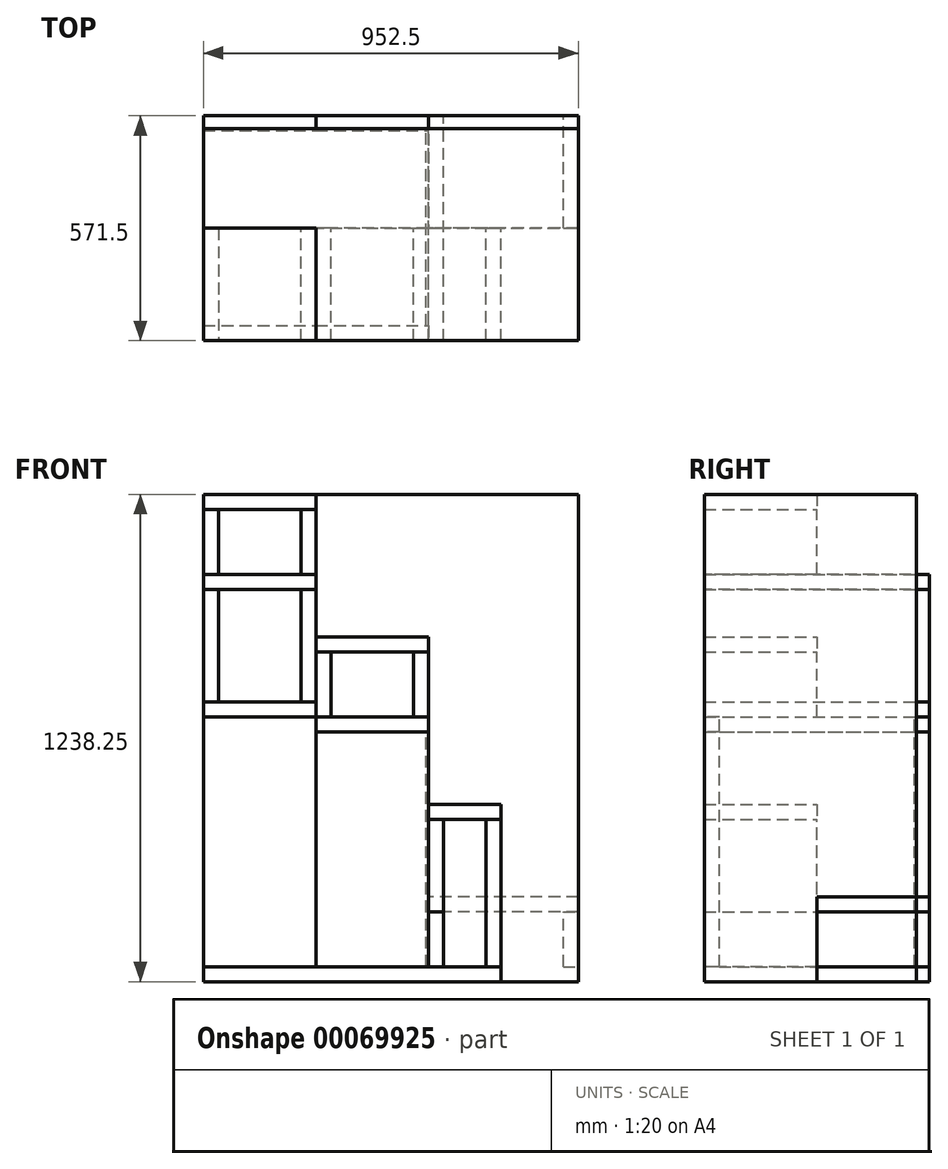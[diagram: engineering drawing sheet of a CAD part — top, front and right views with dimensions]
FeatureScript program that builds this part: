
annotation { "Feature Type Name" : "Feature", "Feature Type Description" : "" }
export const myFeature = defineFeature(function(context is Context, id is Id, definition is map)
    precondition{}
    {
        {
            var Q0;
            Q0=qCreatedBy(makeId("Top.planeOp"),FACE);
            var sketch = newSketch(context, id + "F0", { "sketchPlane" : qUnion([Q0])});
            skLineSegment(sketch, "E0.bottom", {"start": v(-476.25, 269.24) * mm, "end": v(476.25, 269.24) * mm});
            skLineSegment(sketch, "E0.top", {"start": v(-476.25, -269.24) * mm, "end": v(476.25, -269.24) * mm});
            skLineSegment(sketch, "E0.left", {"start": v(-476.25, 269.24) * mm, "end": v(-476.25, -269.24) * mm});
            skLineSegment(sketch, "E0.right", {"start": v(476.25, 269.24) * mm, "end": v(476.25, -269.24) * mm});
            skPoint(sketch, "E0.middle", {"position": v(0, 0) * mm});
            skSolve(sketch);
        }
        {
            var Q0;
            Q0 = qSketchRegion(id + "F0", true);
            extrude(context, id + "F1", {"entities" : qUnion([Q0]), "offsetDistance" : 25.4 * mm, "depth" : 1238.25 * mm});
        }
        {
            var Q0;
            Q0=makeQuery(id+"F1.opExtrude","CAP_FACE",FACE,{"disambiguationData":[OSD([sQuery(id+"F0.wireOp",EDGE,"E0.bottom"),sQuery(id+"F0.wireOp",EDGE,"E0.top"),sQuery(id+"F0.wireOp",EDGE,"E0.left"),sQuery(id+"F0.wireOp",EDGE,"E0.right")])],"isStart":true});
            var sketch = newSketch(context, id + "F2", { "sketchPlane" : qUnion([Q0])});
            skLineSegment(sketch, "E1.bottom", {"start": v(-476.25, 269.24) * mm, "end": v(279.4, 269.24) * mm});
            skLineSegment(sketch, "E1.top", {"start": v(-476.25, -16.5) * mm, "end": v(279.4, -16.5) * mm});
            skLineSegment(sketch, "E1.left", {"start": v(-476.25, 269.24) * mm, "end": v(-476.25, -16.5) * mm});
            skLineSegment(sketch, "E1.right", {"start": v(279.4, 269.24) * mm, "end": v(279.4, -16.5) * mm});
            skSolve(sketch);
        }
        {
            var Q0;
            Q0 = qSketchRegion(id + "F2", true);
            extrude(context, id + "F3", {"entities" : qUnion([Q0]), "oppositeDirection" : true, "depth" : 38.1 * mm, "offsetDistance" : 25.4 * mm});
        }
        {
            var Q0;
            Q0=makeQuery(id+"F1.opExtrude","CAP_FACE",FACE,{"disambiguationData":[OSD([sQuery(id+"F0.wireOp",EDGE,"E0.bottom"),sQuery(id+"F0.wireOp",EDGE,"E0.top"),sQuery(id+"F0.wireOp",EDGE,"E0.left"),sQuery(id+"F0.wireOp",EDGE,"E0.right")])],"isStart":true});
            var sketch = newSketch(context, id + "F4", { "sketchPlane" : qUnion([Q0])});
            skLineSegment(sketch, "E2.bottom", {"start": v(-476.25, -16.5) * mm, "end": v(476.25, -16.5) * mm});
            skLineSegment(sketch, "E2.top", {"start": v(-476.25, -302.26) * mm, "end": v(476.25, -302.26) * mm});
            skLineSegment(sketch, "E2.left", {"start": v(-476.25, -16.5) * mm, "end": v(-476.25, -302.26) * mm});
            skLineSegment(sketch, "E2.right", {"start": v(476.25, -16.5) * mm, "end": v(476.25, -302.26) * mm});
            skSolve(sketch);
        }
        {
            var Q0;
            Q0 = qSketchRegion(id + "F4", true);
            extrude(context, id + "F5", {"entities" : qUnion([Q0]), "oppositeDirection" : true, "depth" : 38.1 * mm, "offsetDistance" : 25.4 * mm});
        }
        {
            var Q0;
            Q0=makeQuery(id+"F5.opExtrude","SWEPT_FACE",FACE,{"disambiguationData":[OSD([sQuery(id+"F4.wireOp",EDGE,"E2.top")])]});
            var sketch = newSketch(context, id + "F6", { "sketchPlane" : qUnion([Q0])});
            skLineSegment(sketch, "E3.bottom", {"start": v(476.25, 38.1) * mm, "end": v(190.5, 38.1) * mm});
            skLineSegment(sketch, "E3.top", {"start": v(476.25, 673.1) * mm, "end": v(190.5, 673.1) * mm});
            skLineSegment(sketch, "E3.left", {"start": v(476.25, 38.1) * mm, "end": v(476.25, 673.1) * mm});
            skLineSegment(sketch, "E3.right", {"start": v(190.5, 38.1) * mm, "end": v(190.5, 673.1) * mm});
            skSolve(sketch);
        }
        {
            var Q0;
            Q0 = qSketchRegion(id + "F6", true);
            extrude(context, id + "F7", {"entities" : qUnion([Q0]), "oppositeDirection" : true, "depth" : 38.1 * mm, "offsetDistance" : 25.4 * mm});
        }
        {
            var Q0;
            Q0=makeQuery(id+"F5.opExtrude","SWEPT_FACE",FACE,{"disambiguationData":[OSD([sQuery(id+"F4.wireOp",EDGE,"E2.top")])]});
            var sketch = newSketch(context, id + "F8", { "sketchPlane" : qUnion([Q0])});
            skLineSegment(sketch, "E4.bottom", {"start": v(190.5, 38.1) * mm, "end": v(-95.25, 38.1) * mm});
            skLineSegment(sketch, "E4.top", {"start": v(190.5, 635) * mm, "end": v(-95.25, 635) * mm});
            skLineSegment(sketch, "E4.left", {"start": v(190.5, 38.1) * mm, "end": v(190.5, 635) * mm});
            skLineSegment(sketch, "E4.right", {"start": v(-95.25, 38.1) * mm, "end": v(-95.25, 635) * mm});
            skSolve(sketch);
        }
        {
            var Q0;
            Q0 = qSketchRegion(id + "F8", true);
            extrude(context, id + "F9", {"entities" : qUnion([Q0]), "oppositeDirection" : true, "depth" : 38.1 * mm, "offsetDistance" : 25.4 * mm});
        }
        {
            var Q0;
            Q0=makeQuery(id+"F3.opExtrude","SWEPT_FACE",FACE,{"disambiguationData":[OSD([sQuery(id+"F2.wireOp",EDGE,"E1.bottom")])]});
            var sketch = newSketch(context, id + "F10", { "sketchPlane" : qUnion([Q0])});
            skLineSegment(sketch, "E5.bottom", {"start": v(-476.25, 38.1) * mm, "end": v(-190.5, 38.1) * mm});
            skLineSegment(sketch, "E5.top", {"start": v(-476.25, 673.1) * mm, "end": v(-190.5, 673.1) * mm});
            skLineSegment(sketch, "E5.left", {"start": v(-476.25, 38.1) * mm, "end": v(-476.25, 673.1) * mm});
            skLineSegment(sketch, "E5.right", {"start": v(-190.5, 38.1) * mm, "end": v(-190.5, 673.1) * mm});
            skSolve(sketch);
        }
        {
            var Q0;
            Q0 = qSketchRegion(id + "F10", true);
            extrude(context, id + "F11", {"entities" : qUnion([Q0]), "oppositeDirection" : true, "depth" : 38.1 * mm, "offsetDistance" : 25.4 * mm});
        }
        {
            var Q0;
            Q0=makeQuery(id+"F3.opExtrude","SWEPT_FACE",FACE,{"disambiguationData":[OSD([sQuery(id+"F2.wireOp",EDGE,"E1.bottom")])]});
            var sketch = newSketch(context, id + "F12", { "sketchPlane" : qUnion([Q0])});
            skLineSegment(sketch, "E6.bottom", {"start": v(-190.5, 38.1) * mm, "end": v(95.25, 38.1) * mm});
            skLineSegment(sketch, "E6.top", {"start": v(-190.5, 635) * mm, "end": v(95.25, 635) * mm});
            skLineSegment(sketch, "E6.left", {"start": v(-190.5, 38.1) * mm, "end": v(-190.5, 635) * mm});
            skLineSegment(sketch, "E6.right", {"start": v(95.25, 38.1) * mm, "end": v(95.25, 635) * mm});
            skSolve(sketch);
        }
        {
            var Q0;
            Q0 = qSketchRegion(id + "F12", true);
            extrude(context, id + "F13", {"entities" : qUnion([Q0]), "oppositeDirection" : true, "depth" : 38.1 * mm, "offsetDistance" : 25.4 * mm});
        }
        {
            var Q0;
            Q0=makeQuery(id+"F13.opExtrude","SWEPT_FACE",FACE,{"disambiguationData":[OSD([sQuery(id+"F12.wireOp",EDGE,"E6.right")])]});
            var sketch = newSketch(context, id + "F14", { "sketchPlane" : qUnion([Q0])});
            skLineSegment(sketch, "E7.bottom", {"start": v(-269.24, 38.1) * mm, "end": v(302.26, 38.1) * mm});
            skLineSegment(sketch, "E7.top", {"start": v(-269.24, 177.8) * mm, "end": v(302.26, 177.8) * mm});
            skLineSegment(sketch, "E7.left", {"start": v(-269.24, 38.1) * mm, "end": v(-269.24, 177.8) * mm});
            skLineSegment(sketch, "E7.right", {"start": v(302.26, 38.1) * mm, "end": v(302.26, 177.8) * mm});
            skSolve(sketch);
        }
        {
            var Q0;
            Q0 = qSketchRegion(id + "F14", true);
            extrude(context, id + "F15", {"entities" : qUnion([Q0]), "depth" : 38.1 * mm, "offsetDistance" : 25.4 * mm});
        }
        {
            var Q0;
            Q0=makeQuery(id+"F3.opExtrude","SWEPT_FACE",FACE,{"disambiguationData":[OSD([sQuery(id+"F2.wireOp",EDGE,"E1.right")])]});
            var sketch = newSketch(context, id + "F16", { "sketchPlane" : qUnion([Q0])});
            skLineSegment(sketch, "E8.bottom", {"start": v(-269.24, 38.1) * mm, "end": v(16.5, 38.1) * mm});
            skLineSegment(sketch, "E8.top", {"start": v(-269.24, 412.75) * mm, "end": v(16.5, 412.75) * mm});
            skLineSegment(sketch, "E8.left", {"start": v(-269.24, 38.1) * mm, "end": v(-269.24, 412.75) * mm});
            skLineSegment(sketch, "E8.right", {"start": v(16.51, 38.1) * mm, "end": v(16.5, 412.75) * mm});
            skSolve(sketch);
        }
        {
            var Q0;
            Q0 = qSketchRegion(id + "F16", true);
            extrude(context, id + "F17", {"entities" : qUnion([Q0]), "oppositeDirection" : true, "depth" : 38.1 * mm, "offsetDistance" : 25.4 * mm});
        }
        {
            var Q0;
            Q0=makeQuery(id+"F5.opExtrude","SWEPT_FACE",FACE,{"disambiguationData":[OSD([sQuery(id+"F4.wireOp",EDGE,"E2.right")])]});
            var sketch = newSketch(context, id + "F18", { "sketchPlane" : qUnion([Q0])});
            skLineSegment(sketch, "E9.bottom", {"start": v(16.5, 38.1) * mm, "end": v(302.26, 38.1) * mm});
            skLineSegment(sketch, "E9.top", {"start": v(16.5, 177.8) * mm, "end": v(302.26, 177.8) * mm});
            skLineSegment(sketch, "E9.left", {"start": v(16.5, 38.1) * mm, "end": v(16.5, 177.8) * mm});
            skLineSegment(sketch, "E9.right", {"start": v(302.26, 38.1) * mm, "end": v(302.26, 177.8) * mm});
            skSolve(sketch);
        }
        {
            var Q0;
            Q0 = qSketchRegion(id + "F18", true);
            extrude(context, id + "F19", {"entities" : qUnion([Q0]), "oppositeDirection" : true, "depth" : 38.1 * mm, "offsetDistance" : 25.4 * mm});
        }
        {
            var Q0;
            Q0=makeQuery(id+"F19.opExtrude","SWEPT_FACE",FACE,{"disambiguationData":[OSD([sQuery(id+"F18.wireOp",EDGE,"E9.top")])]});
            var sketch = newSketch(context, id + "F20", { "sketchPlane" : qUnion([Q0])});
            skLineSegment(sketch, "E10.bottom", {"start": v(476.25, 302.26) * mm, "end": v(95.25, 302.26) * mm});
            skLineSegment(sketch, "E10.top", {"start": v(476.25, 16.5) * mm, "end": v(95.25, 16.5) * mm});
            skLineSegment(sketch, "E10.left", {"start": v(476.25, 302.26) * mm, "end": v(476.25, 16.5) * mm});
            skLineSegment(sketch, "E10.right", {"start": v(95.25, 302.26) * mm, "end": v(95.25, 16.5) * mm});
            skSolve(sketch);
        }
        {
            var Q0;
            Q0 = qSketchRegion(id + "F20", true);
            extrude(context, id + "F21", {"entities" : qUnion([Q0]), "depth" : 38.1 * mm, "offsetDistance" : 25.4 * mm});
        }
        {
            var Q0;
            Q0=makeQuery(id+"F15.opExtrude","CAP_FACE",FACE,{"disambiguationData":[OSD([sQuery(id+"F14.wireOp",EDGE,"E7.bottom"),sQuery(id+"F14.wireOp",EDGE,"E7.top"),sQuery(id+"F14.wireOp",EDGE,"E7.left"),sQuery(id+"F14.wireOp",EDGE,"E7.right")])],"isStart":false});
            var sketch = newSketch(context, id + "F22", { "sketchPlane" : qUnion([Q0])});
            skLineSegment(sketch, "E11.bottom", {"start": v(-269.24, 177.8) * mm, "end": v(16.5, 177.8) * mm});
            skLineSegment(sketch, "E11.top", {"start": v(-269.24, 412.75) * mm, "end": v(16.5, 412.75) * mm});
            skLineSegment(sketch, "E11.left", {"start": v(-269.24, 177.8) * mm, "end": v(-269.24, 412.75) * mm});
            skLineSegment(sketch, "E11.right", {"start": v(16.5, 177.8) * mm, "end": v(16.5, 412.75) * mm});
            skSolve(sketch);
        }
        {
            var Q0;
            Q0 = qSketchRegion(id + "F22", true);
            extrude(context, id + "F23", {"entities" : qUnion([Q0]), "oppositeDirection" : true, "depth" : 38.1 * mm, "offsetDistance" : 25.4 * mm});
        }
        {
            var Q0;
            Q0=makeQuery(id+"F17.opExtrude","SWEPT_FACE",FACE,{"disambiguationData":[OSD([sQuery(id+"F16.wireOp",EDGE,"E8.top")])]});
            var sketch = newSketch(context, id + "F24", { "sketchPlane" : qUnion([Q0])});
            skLineSegment(sketch, "E12.bottom", {"start": v(279.4, -269.24) * mm, "end": v(95.25, -269.24) * mm});
            skLineSegment(sketch, "E12.top", {"start": v(279.4, 16.5) * mm, "end": v(95.25, 16.5) * mm});
            skLineSegment(sketch, "E12.left", {"start": v(279.4, -269.24) * mm, "end": v(279.4, 16.5) * mm});
            skLineSegment(sketch, "E12.right", {"start": v(95.25, -269.24) * mm, "end": v(95.25, 16.5) * mm});
            skSolve(sketch);
        }
        {
            var Q0;
            Q0 = qSketchRegion(id + "F24", true);
            extrude(context, id + "F25", {"entities" : qUnion([Q0]), "depth" : 38.1 * mm, "offsetDistance" : 25.4 * mm});
        }
        {
            var Q0;
            Q0=makeQuery(id+"F9.opExtrude","SWEPT_FACE",FACE,{"disambiguationData":[OSD([sQuery(id+"F8.wireOp",EDGE,"E4.top")])]});
            var sketch = newSketch(context, id + "F26", { "sketchPlane" : qUnion([Q0])});
            skLineSegment(sketch, "E13.bottom", {"start": v(95.25, 302.26) * mm, "end": v(-190.5, 302.26) * mm});
            skLineSegment(sketch, "E13.top", {"start": v(95.25, -269.24) * mm, "end": v(-190.5, -269.24) * mm});
            skLineSegment(sketch, "E13.left", {"start": v(95.25, 302.26) * mm, "end": v(95.25, -269.24) * mm});
            skLineSegment(sketch, "E13.right", {"start": v(-190.5, 302.26) * mm, "end": v(-190.5, -269.24) * mm});
            skSolve(sketch);
        }
        {
            var Q0;
            Q0 = qSketchRegion(id + "F26", true);
            extrude(context, id + "F27", {"entities" : qUnion([Q0]), "depth" : 38.1 * mm, "offsetDistance" : 25.4 * mm});
        }
        {
            var Q0;
            Q0=makeQuery(id+"F7.opExtrude","SWEPT_FACE",FACE,{"disambiguationData":[OSD([sQuery(id+"F6.wireOp",EDGE,"E3.top")])]});
            var sketch = newSketch(context, id + "F28", { "sketchPlane" : qUnion([Q0])});
            skLineSegment(sketch, "E14.bottom", {"start": v(-190.5, 302.26) * mm, "end": v(-476.25, 302.26) * mm});
            skLineSegment(sketch, "E14.top", {"start": v(-190.5, -269.24) * mm, "end": v(-476.25, -269.24) * mm});
            skLineSegment(sketch, "E14.left", {"start": v(-190.5, 302.26) * mm, "end": v(-190.5, -269.24) * mm});
            skLineSegment(sketch, "E14.right", {"start": v(-476.25, 302.26) * mm, "end": v(-476.25, -269.24) * mm});
            skSolve(sketch);
        }
        {
            var Q0;
            Q0 = qSketchRegion(id + "F28", true);
            extrude(context, id + "F29", {"entities" : qUnion([Q0]), "depth" : 38.1 * mm, "offsetDistance" : 25.4 * mm});
        }
        {
            var Q0;
            Q0=makeQuery(id+"F27.opExtrude","SWEPT_FACE",FACE,{"disambiguationData":[OSD([sQuery(id+"F26.wireOp",EDGE,"E13.left")])]});
            var sketch = newSketch(context, id + "F30", { "sketchPlane" : qUnion([Q0])});
            skLineSegment(sketch, "E15.bottom", {"start": v(-269.24, 673.1) * mm, "end": v(16.5, 673.1) * mm});
            skLineSegment(sketch, "E15.top", {"start": v(-269.24, 838.2) * mm, "end": v(16.5, 838.2) * mm});
            skLineSegment(sketch, "E15.left", {"start": v(-269.24, 673.1) * mm, "end": v(-269.24, 838.2) * mm});
            skLineSegment(sketch, "E15.right", {"start": v(16.5, 673.1) * mm, "end": v(16.5, 838.2) * mm});
            skSolve(sketch);
        }
        {
            var Q0;
            Q0 = qSketchRegion(id + "F30", true);
            extrude(context, id + "F31", {"entities" : qUnion([Q0]), "oppositeDirection" : true, "depth" : 38.1 * mm, "offsetDistance" : 25.4 * mm});
        }
        {
            var Q0;
            Q0=makeQuery(id+"F27.opExtrude","SWEPT_FACE",FACE,{"disambiguationData":[OSD([sQuery(id+"F26.wireOp",EDGE,"E13.right")])]});
            var sketch = newSketch(context, id + "F32", { "sketchPlane" : qUnion([Q0])});
            skLineSegment(sketch, "E16.bottom", {"start": v(269.24, 673.1) * mm, "end": v(-16.5, 673.1) * mm});
            skLineSegment(sketch, "E16.top", {"start": v(269.24, 838.2) * mm, "end": v(-16.5, 838.2) * mm});
            skLineSegment(sketch, "E16.left", {"start": v(269.24, 673.1) * mm, "end": v(269.24, 838.2) * mm});
            skLineSegment(sketch, "E16.right", {"start": v(-16.5, 673.1) * mm, "end": v(-16.5, 838.2) * mm});
            skSolve(sketch);
        }
        {
            var Q0;
            Q0 = qSketchRegion(id + "F32", true);
            extrude(context, id + "F33", {"entities" : qUnion([Q0]), "oppositeDirection" : true, "depth" : 38.1 * mm, "offsetDistance" : 25.4 * mm});
        }
        {
            var Q0;
            Q0=makeQuery(id+"F31.opExtrude","SWEPT_FACE",FACE,{"disambiguationData":[OSD([sQuery(id+"F30.wireOp",EDGE,"E15.top")])]});
            var sketch = newSketch(context, id + "F34", { "sketchPlane" : qUnion([Q0])});
            skLineSegment(sketch, "E17.bottom", {"start": v(95.25, -269.24) * mm, "end": v(-190.5, -269.24) * mm});
            skLineSegment(sketch, "E17.top", {"start": v(95.25, 16.5) * mm, "end": v(-190.5, 16.5) * mm});
            skLineSegment(sketch, "E17.left", {"start": v(95.25, -269.24) * mm, "end": v(95.25, 16.5) * mm});
            skLineSegment(sketch, "E17.right", {"start": v(-190.5, -269.24) * mm, "end": v(-190.5, 16.5) * mm});
            skSolve(sketch);
        }
        {
            var Q0;
            Q0 = qSketchRegion(id + "F34", true);
            extrude(context, id + "F35", {"entities" : qUnion([Q0]), "depth" : 38.1 * mm, "offsetDistance" : 25.4 * mm});
        }
        {
            var Q0;
            Q0=makeQuery(id+"F7.opExtrude","SWEPT_FACE",FACE,{"disambiguationData":[OSD([sQuery(id+"F6.wireOp",EDGE,"E3.top")])]});
            var sketch = newSketch(context, id + "F36", { "sketchPlane" : qUnion([Q0])});
            skLineSegment(sketch, "E18.bottom", {"start": v(-476.25, 302.26) * mm, "end": v(-190.5, 302.26) * mm});
            skLineSegment(sketch, "E18.top", {"start": v(-476.25, -269.24) * mm, "end": v(-190.5, -269.24) * mm});
            skLineSegment(sketch, "E18.left", {"start": v(-476.25, 302.26) * mm, "end": v(-476.25, -269.24) * mm});
            skLineSegment(sketch, "E18.right", {"start": v(-190.5, 302.26) * mm, "end": v(-190.5, -269.24) * mm});
            skSolve(sketch);
        }
        {
            var Q0;
            Q0 = qSketchRegion(id + "F36", true);
            extrude(context, id + "F37", {"entities" : qUnion([Q0]), "depth" : 38.1 * mm, "offsetDistance" : 25.4 * mm});
        }
        {
            var Q0;
            Q0=makeQuery(id+"F37.opExtrude","CAP_FACE",FACE,{"disambiguationData":[OSD([sQuery(id+"F36.wireOp",EDGE,"E18.bottom"),sQuery(id+"F36.wireOp",EDGE,"E18.top"),sQuery(id+"F36.wireOp",EDGE,"E18.left"),sQuery(id+"F36.wireOp",EDGE,"E18.right")])],"isStart":false});
            var sketch = newSketch(context, id + "F38", { "sketchPlane" : qUnion([Q0])});
            skLineSegment(sketch, "E19.bottom", {"start": v(-190.5, 302.26) * mm, "end": v(-228.6, 302.26) * mm});
            skLineSegment(sketch, "E19.top", {"start": v(-190.5, -269.24) * mm, "end": v(-228.6, -269.24) * mm});
            skLineSegment(sketch, "E19.left", {"start": v(-190.5, 302.26) * mm, "end": v(-190.5, -269.24) * mm});
            skLineSegment(sketch, "E19.right", {"start": v(-228.6, 302.26) * mm, "end": v(-228.6, -269.24) * mm});
            skSolve(sketch);
        }
        {
            var Q0;
            Q0 = qSketchRegion(id + "F38", true);
            extrude(context, id + "F39", {"entities" : qUnion([Q0]), "depth" : 285.75 * mm, "offsetDistance" : 25.4 * mm});
        }
        {
            var Q0;
            Q0=makeQuery(id+"F37.opExtrude","SWEPT_FACE",FACE,{"disambiguationData":[OSD([sQuery(id+"F36.wireOp",EDGE,"E18.left")])]});
            var sketch = newSketch(context, id + "F40", { "sketchPlane" : qUnion([Q0])});
            skLineSegment(sketch, "E20.bottom", {"start": v(-302.26, 711.2) * mm, "end": v(269.24, 711.2) * mm});
            skLineSegment(sketch, "E20.top", {"start": v(-302.26, 996.95) * mm, "end": v(269.24, 996.95) * mm});
            skLineSegment(sketch, "E20.left", {"start": v(-302.26, 711.2) * mm, "end": v(-302.26, 996.95) * mm});
            skLineSegment(sketch, "E20.right", {"start": v(269.24, 711.2) * mm, "end": v(269.24, 996.95) * mm});
            skSolve(sketch);
        }
        {
            var Q0;
            Q0 = qSketchRegion(id + "F40", true);
            extrude(context, id + "F41", {"entities" : qUnion([Q0]), "oppositeDirection" : true, "depth" : 38.1 * mm, "offsetDistance" : 25.4 * mm});
        }
        {
            var Q0;
            Q0=makeQuery(id+"F39.opExtrude","CAP_FACE",FACE,{"disambiguationData":[OSD([sQuery(id+"F38.wireOp",EDGE,"E19.bottom"),sQuery(id+"F38.wireOp",EDGE,"E19.top"),sQuery(id+"F38.wireOp",EDGE,"E19.left"),sQuery(id+"F38.wireOp",EDGE,"E19.right")])],"isStart":false});
            var sketch = newSketch(context, id + "F42", { "sketchPlane" : qUnion([Q0])});
            skLineSegment(sketch, "E21.bottom", {"start": v(-190.5, 302.26) * mm, "end": v(-476.25, 302.26) * mm});
            skLineSegment(sketch, "E21.top", {"start": v(-190.5, -269.24) * mm, "end": v(-476.25, -269.24) * mm});
            skLineSegment(sketch, "E21.left", {"start": v(-190.5, 302.26) * mm, "end": v(-190.5, -269.24) * mm});
            skLineSegment(sketch, "E21.right", {"start": v(-476.25, 302.26) * mm, "end": v(-476.25, -269.24) * mm});
            skSolve(sketch);
        }
        {
            var Q0;
            Q0 = qSketchRegion(id + "F42", true);
            extrude(context, id + "F43", {"entities" : qUnion([Q0]), "depth" : 38.1 * mm, "offsetDistance" : 25.4 * mm});
        }
        {
            var Q0;
            Q0=makeQuery(id+"F43.opExtrude","SWEPT_FACE",FACE,{"disambiguationData":[OSD([sQuery(id+"F42.wireOp",EDGE,"E21.left")])]});
            var sketch = newSketch(context, id + "F44", { "sketchPlane" : qUnion([Q0])});
            skLineSegment(sketch, "E22.bottom", {"start": v(-269.24, 1035.05) * mm, "end": v(16.5, 1035.05) * mm});
            skLineSegment(sketch, "E22.top", {"start": v(-269.24, 1200.15) * mm, "end": v(16.5, 1200.15) * mm});
            skLineSegment(sketch, "E22.left", {"start": v(-269.24, 1035.05) * mm, "end": v(-269.24, 1200.15) * mm});
            skLineSegment(sketch, "E22.right", {"start": v(16.5, 1035.05) * mm, "end": v(16.5, 1200.15) * mm});
            skSolve(sketch);
        }
        {
            var Q0;
            Q0 = qSketchRegion(id + "F44", true);
            extrude(context, id + "F45", {"entities" : qUnion([Q0]), "oppositeDirection" : true, "depth" : 38.1 * mm, "offsetDistance" : 25.4 * mm});
        }
        {
            var Q0;
            Q0=makeQuery(id+"F43.opExtrude","SWEPT_FACE",FACE,{"disambiguationData":[OSD([sQuery(id+"F42.wireOp",EDGE,"E21.right")])]});
            var sketch = newSketch(context, id + "F46", { "sketchPlane" : qUnion([Q0])});
            skLineSegment(sketch, "E23.bottom", {"start": v(269.24, 1035.05) * mm, "end": v(-16.5, 1035.05) * mm});
            skLineSegment(sketch, "E23.top", {"start": v(269.24, 1200.15) * mm, "end": v(-16.5, 1200.15) * mm});
            skLineSegment(sketch, "E23.left", {"start": v(269.24, 1035.05) * mm, "end": v(269.24, 1200.15) * mm});
            skLineSegment(sketch, "E23.right", {"start": v(-16.5, 1035.05) * mm, "end": v(-16.5, 1200.15) * mm});
            skSolve(sketch);
        }
        {
            var Q0;
            Q0 = qSketchRegion(id + "F46", true);
            extrude(context, id + "F47", {"entities" : qUnion([Q0]), "oppositeDirection" : true, "depth" : 38.1 * mm, "offsetDistance" : 25.4 * mm});
        }
        {
            var Q0;
            Q0=makeQuery(id+"F47.opExtrude","SWEPT_FACE",FACE,{"disambiguationData":[OSD([sQuery(id+"F46.wireOp",EDGE,"E23.top")])]});
            var sketch = newSketch(context, id + "F48", { "sketchPlane" : qUnion([Q0])});
            skLineSegment(sketch, "E24.bottom", {"start": v(-476.25, 16.5) * mm, "end": v(-190.5, 16.5) * mm});
            skLineSegment(sketch, "E24.top", {"start": v(-476.25, -269.24) * mm, "end": v(-190.5, -269.24) * mm});
            skLineSegment(sketch, "E24.left", {"start": v(-476.25, 16.5) * mm, "end": v(-476.25, -269.24) * mm});
            skLineSegment(sketch, "E24.right", {"start": v(-190.5, 16.5) * mm, "end": v(-190.5, -269.24) * mm});
            skSolve(sketch);
        }
        {
            var Q0;
            Q0 = qSketchRegion(id + "F48", true);
            extrude(context, id + "F49", {"entities" : qUnion([Q0]), "depth" : 38.1 * mm, "offsetDistance" : 25.4 * mm});
        }
        {
            var Q0;
            Q0=makeQuery(id+"F15.opExtrude","CAP_FACE",FACE,{"disambiguationData":[OSD([sQuery(id+"F14.wireOp",EDGE,"E7.bottom"),sQuery(id+"F14.wireOp",EDGE,"E7.top"),sQuery(id+"F14.wireOp",EDGE,"E7.left"),sQuery(id+"F14.wireOp",EDGE,"E7.right")])],"isStart":true});
            var sketch = newSketch(context, id + "F50", { "sketchPlane" : qUnion([Q0])});
            skLineSegment(sketch, "E25.bottom", {"start": v(231.14, 38.1) * mm, "end": v(-264.16, 38.1) * mm});
            skLineSegment(sketch, "E25.top", {"start": v(231.14, 635) * mm, "end": v(-264.16, 635) * mm});
            skLineSegment(sketch, "E25.left", {"start": v(231.14, 38.1) * mm, "end": v(231.14, 635) * mm});
            skLineSegment(sketch, "E25.right", {"start": v(-264.16, 38.1) * mm, "end": v(-264.16, 635) * mm});
            skSolve(sketch);
        }
        {
            var Q0;
            Q0 = qSketchRegion(id + "F50", true);
            extrude(context, id + "F51", {"entities" : qUnion([Q0]), "depth" : 6.35 * mm, "offsetDistance" : 25.4 * mm});
        }
    });
